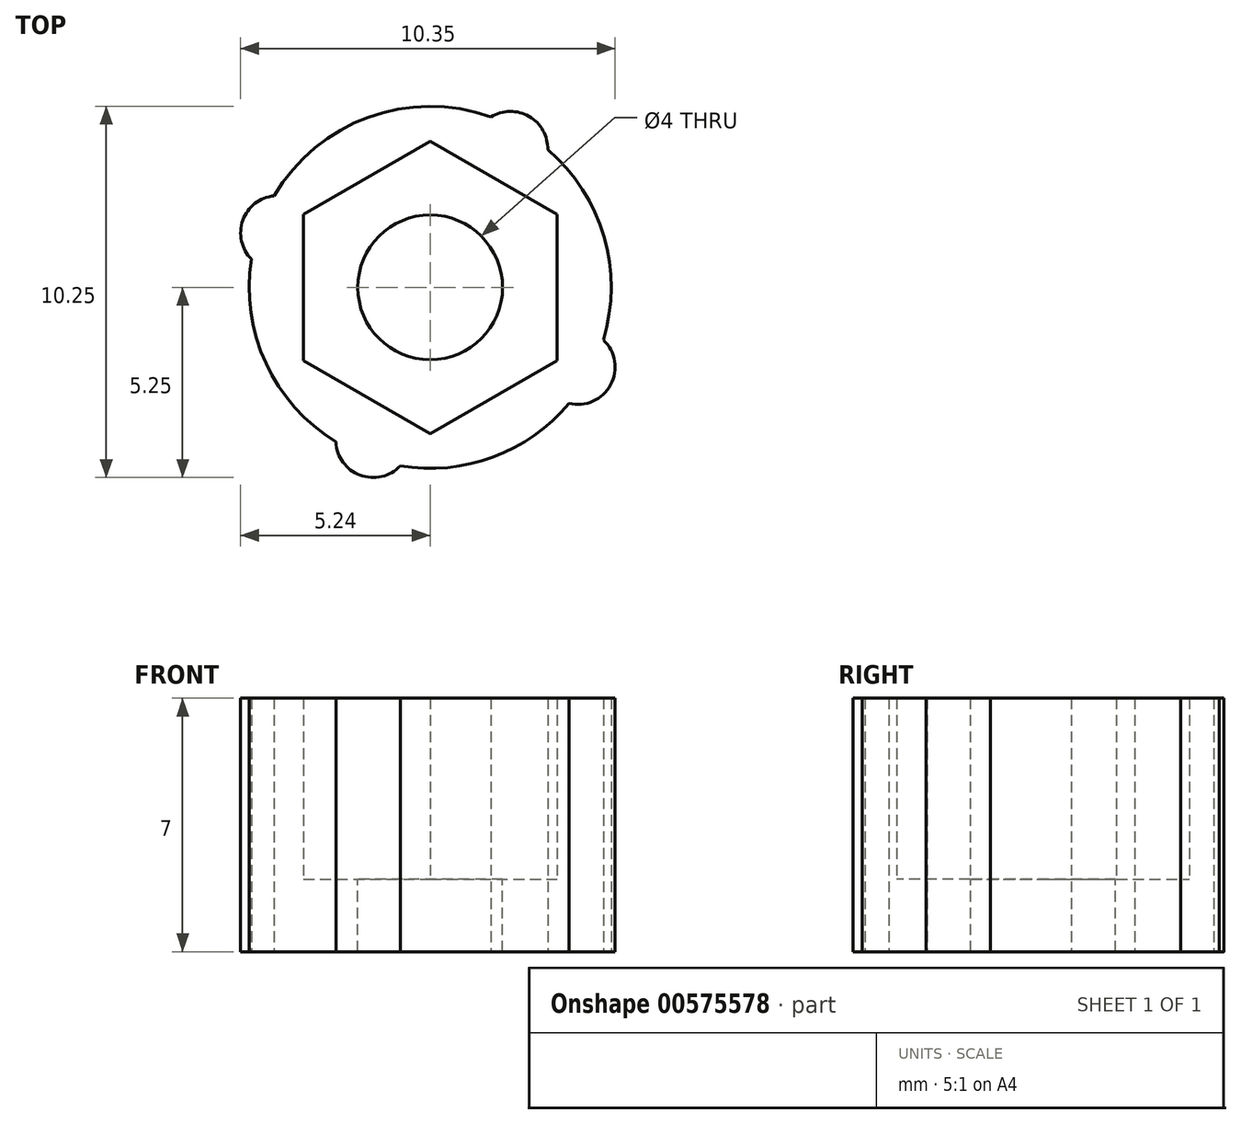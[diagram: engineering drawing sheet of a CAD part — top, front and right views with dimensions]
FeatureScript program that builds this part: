
annotation { "Feature Type Name" : "Feature", "Feature Type Description" : "" }
export const myFeature = defineFeature(function(context is Context, id is Id, definition is map)
    precondition{}
    {
        {
            var Q0;
            Q0=qCreatedBy(makeId("Top.planeOp"),FACE);
            var sketch = newSketch(context, id + "F0", { "sketchPlane" : qUnion([Q0])});
            skCircle(sketch, "E0", {"center": v(0, 0) * mm, "radius": 5 * mm});
            skCircle(sketch, "E1.cCircle", {"center": v(0, 0) * mm, "radius": 3.5 * mm, "construction": true});
            skLineSegment(sketch, "E1.0", {"start": v(-3.5, 2.02) * mm, "end": v(0, 4.04) * mm});
            skLineSegment(sketch, "E1.1", {"start": v(0, 4.04) * mm, "end": v(3.5, 2.02) * mm});
            skLineSegment(sketch, "E1.2", {"start": v(3.5, 2.02) * mm, "end": v(3.5, -2.02) * mm});
            skLineSegment(sketch, "E1.3", {"start": v(3.5, -2.02) * mm, "end": v(0, -4.04) * mm});
            skLineSegment(sketch, "E1.4", {"start": v(0, -4.04) * mm, "end": v(-3.5, -2.02) * mm});
            skLineSegment(sketch, "E1.5", {"start": v(-3.5, -2.02) * mm, "end": v(-3.5, 2.02) * mm});
            skPoint(sketch, "E1.0.midPoint", {"position": v(-1.75, 3.03) * mm});
            skCircle(sketch, "E2", {"center": v(0, 0) * mm, "radius": 2 * mm});
            skArc(sketch, "E3", {"start": v(3.84, -3.2) * mm, "mid": v(4.98, -2.7) * mm, "end": v(4.78, -1.45) * mm});
            skArc(sketch, "E4", {"start": v(-2.6, -4.27) * mm, "mid": v(-1.94, -5.19) * mm, "end": v(-0.83, -4.93) * mm});
            skArc(sketch, "E5", {"start": v(-4.31, 2.53) * mm, "mid": v(-5.18, 1.85) * mm, "end": v(-4.94, 0.78) * mm});
            skArc(sketch, "E6", {"start": v(3.25, 3.8) * mm, "mid": v(2.73, 4.72) * mm, "end": v(1.68, 4.7) * mm});
            skSolve(sketch);
        }
        {
            var Q0;
            Q0=makeQuery(id+"F0.imprint","IMPRINT",FACE,{"disambiguationData":[TD([[makeQuery(id+"F0.imprint","IMPRINT",EDGE,{"derivedFrom":sQuery(id+"F0.wireOp",EDGE,"E0")}),1.0]])]});
            var Q1;
            {var subQ0=sQuery(id+"F0.wireOp",EDGE,"E3");Q1=makeQuery(id+"F0.imprint","IMPRINT",FACE,{"disambiguationData":[TD([[makeQuery(id+"F0.imprint","IMPRINT",EDGE,{"derivedFrom":subQ0}),1.0]])]});}
            var Q2;
            {var subQ0=sQuery(id+"F0.wireOp",EDGE,"E6");Q2=makeQuery(id+"F0.imprint","IMPRINT",FACE,{"disambiguationData":[TD([[makeQuery(id+"F0.imprint","IMPRINT",EDGE,{"derivedFrom":subQ0}),1.0]])]});}
            var Q3;
            {var subQ0=sQuery(id+"F0.wireOp",EDGE,"E5");Q3=makeQuery(id+"F0.imprint","IMPRINT",FACE,{"disambiguationData":[TD([[makeQuery(id+"F0.imprint","IMPRINT",EDGE,{"derivedFrom":subQ0}),1.0]])]});}
            var Q4;
            {var subQ0=sQuery(id+"F0.wireOp",EDGE,"E4");Q4=makeQuery(id+"F0.imprint","IMPRINT",FACE,{"disambiguationData":[TD([[makeQuery(id+"F0.imprint","IMPRINT",EDGE,{"derivedFrom":subQ0}),1.0]])]});}
            extrude(context, id + "F1", {"entities" : qUnion([Q0, Q1, Q2, Q3, Q4]), "depth" : 5 * mm, "offsetDistance" : 25 * mm});
        }
        {
            var Q0;
            Q0=makeQuery(id+"F0.imprint","IMPRINT",FACE,{"disambiguationData":[TD([[makeQuery(id+"F0.imprint","IMPRINT",EDGE,{"derivedFrom":sQuery(id+"F0.wireOp",EDGE,"E0")}),1.0]])]});
            var Q1;
            Q1=makeQuery(id+"F0.imprint","IMPRINT",FACE,{"disambiguationData":[TD([[makeQuery(id+"F0.imprint","IMPRINT",EDGE,{"derivedFrom":sQuery(id+"F0.wireOp",EDGE,"E1.0")}),-1.0]])]});
            var Q2;
            {var subQ0=sQuery(id+"F0.wireOp",EDGE,"E5");Q2=makeQuery(id+"F0.imprint","IMPRINT",FACE,{"disambiguationData":[TD([[makeQuery(id+"F0.imprint","IMPRINT",EDGE,{"derivedFrom":subQ0}),1.0]])]});}
            var Q3;
            {var subQ0=sQuery(id+"F0.wireOp",EDGE,"E4");Q3=makeQuery(id+"F0.imprint","IMPRINT",FACE,{"disambiguationData":[TD([[makeQuery(id+"F0.imprint","IMPRINT",EDGE,{"derivedFrom":subQ0}),1.0]])]});}
            var Q4;
            {var subQ0=sQuery(id+"F0.wireOp",EDGE,"E3");Q4=makeQuery(id+"F0.imprint","IMPRINT",FACE,{"disambiguationData":[TD([[makeQuery(id+"F0.imprint","IMPRINT",EDGE,{"derivedFrom":subQ0}),1.0]])]});}
            var Q5;
            {var subQ0=sQuery(id+"F0.wireOp",EDGE,"E6");Q5=makeQuery(id+"F0.imprint","IMPRINT",FACE,{"disambiguationData":[TD([[makeQuery(id+"F0.imprint","IMPRINT",EDGE,{"derivedFrom":subQ0}),1.0]])]});}
            extrude(context, id + "F2", {"entities" : qUnion([Q0, Q1, Q2, Q3, Q4, Q5]), "operationType" : NewBodyOperationType.ADD, "oppositeDirection" : true, "depth" : 2 * mm, "offsetDistance" : 25 * mm});
        }
    });
